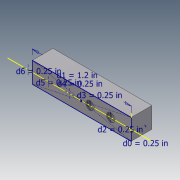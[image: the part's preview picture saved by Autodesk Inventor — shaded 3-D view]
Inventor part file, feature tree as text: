
AUTODESK INVENTOR PART (.ipt)
format: ipt  version: 2020.4 (Build 244396000, 396)  size: 121,856 bytes
history: native  units: in
note: dims shown in document units (in); Inventor stores cm internally (conversion verified against a paired STEP export)
features: hole x3, sketch x2, extrude x1, fillet x1, projected_geometry x1
ambient origin geometry x8: Origin, YZ Plane, XZ Plane, XY Plane, X Axis, Y Axis, Z Axis, Center Point
bodies: Solid1 (feature_tree)
feature tree (8):
  sketch  "Sketch1"  dims[d0=0.25in d1=1.2in]
  extrude  "Extrusion1"  Depth=1.2in
  hole  "Hole1"  [1 undecoded]
  hole  "Hole2"  [1 undecoded]
  fillet  "Fillet1"  Radius=0.25in
  hole  "Hole3"  [1 undecoded]
  sketch  "Sketch2"  dims[d2=0.25in d3=0.25in d4=0.25in d5=0.25in d6=0.25in d7=0.25in d8=0.0in d9=0.104in d10=0.276in d11=0.281in d12=0.138in d13=0.5635in d14=0.432in d15=0.8108in d16=0.06in d17=0.276in d18=0.281in d19=0.138in d20=0.5635in d21=0.432in d22=0.8108in d23=0.125in d24=0.13in d25=0.35in d26=0.375in d27=0.25in d28=0.5635in d29=0.5in d30=0.8108in]
  projected_geometry  "Projected Loop1"
note: 3 required parameter values undecoded (feature->parameter linkage not recoverable at this tier; creation-order binding heuristic only, values carry confidence <= 0.55)
